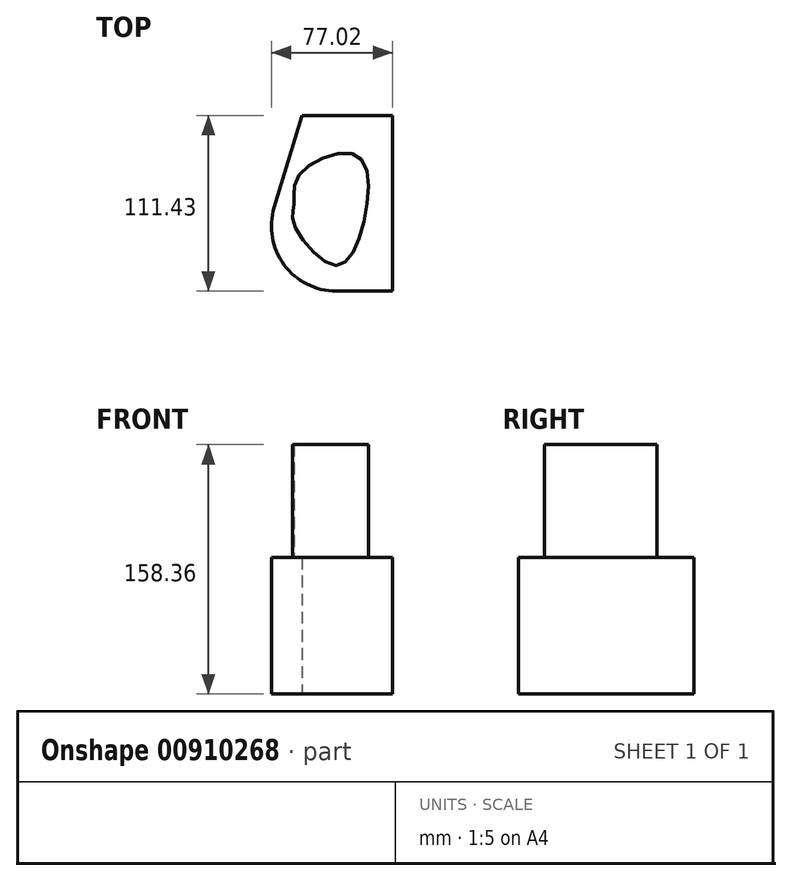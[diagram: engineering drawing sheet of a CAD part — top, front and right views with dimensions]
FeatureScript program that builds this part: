
annotation { "Feature Type Name" : "Feature", "Feature Type Description" : "" }
export const myFeature = defineFeature(function(context is Context, id is Id, definition is map)
    precondition{}
    {
        {
            var Q0;
            Q0=qCreatedBy(makeId("Top.planeOp"),FACE);
            var sketch = newSketch(context, id + "F0", { "sketchPlane" : qUnion([Q0])});
            skLineSegment(sketch, "E0", {"start": v(-54.44, -43.5) * mm, "end": v(36.9, -43.5) * mm});
            skLineSegment(sketch, "E1", {"start": v(36.9, -43.5) * mm, "end": v(36.9, 67.94) * mm});
            skLineSegment(sketch, "E2", {"start": v(36.9, 67.94) * mm, "end": v(-20.7, 67.94) * mm});
            skLineSegment(sketch, "E3", {"start": v(-20.7, 67.94) * mm, "end": v(-54.44, -43.5) * mm});
            skSolve(sketch);
        }
        {
            var Q0;
            Q0 = qSketchRegion(id + "F0", true);
            extrude(context, id + "F1", {"entities" : qUnion([Q0]), "depth" : 86.6 * mm, "offsetDistance" : 25.4 * mm});
        }
        {
            var Q0;
            Q0=makeQuery(id+"F1.opExtrude","SWEPT_EDGE",EDGE,{"disambiguationData":[OSD([sQuery(id+"F0.wireOp",EDGE,"E0"),sQuery(id+"F0.wireOp",EDGE,"E3")])]});
            fillet(context, id + "F2", {"entities" : qUnion([Q0]), "radius" : 41.2 * mm, "tangentPropagation" : true, "allowEdgeOverflow" : false});
        }
        {
            var Q0;
            Q0=makeQuery(id+"F1.opExtrude","CAP_FACE",FACE,{"disambiguationData":[OSD([sQuery(id+"F0.wireOp",EDGE,"E0"),sQuery(id+"F0.wireOp",EDGE,"E1"),sQuery(id+"F0.wireOp",EDGE,"E2"),sQuery(id+"F0.wireOp",EDGE,"E3")])],"isStart":false});
            var sketch = newSketch(context, id + "F3", { "sketchPlane" : qUnion([Q0])});
            skFitSpline(sketch, "E4", {"points": [v(-25.74, 11.32) * mm, v(-26, 0) * mm, v(0, -27.14) * mm, v(18.43, 0) * mm, v(13.81, 42.79) * mm, v(-22.64, 29.97) * mm, v(-25.74, 11.32) * mm]});
            skFitSpline(sketch, "E5", {"points": [v(0, 0) * mm, v(17.07, 67.94) * mm], "startDerivative": vector(17.07, 67.94) * mm, "endDerivative": vector(17.07, 67.94) * mm});
            skSolve(sketch);
        }
        {
            var Q0;
            Q0=makeQuery(id+"F3.imprint","IMPRINT",FACE,{"disambiguationData":[TD([[makeQuery(id+"F3.imprint","IMPRINT",EDGE,{"derivedFrom":sQuery(id+"F3.wireOp",EDGE,"E4")}),1.0]])]});
            extrude(context, id + "F4", {"entities" : qUnion([Q0]), "operationType" : NewBodyOperationType.ADD, "depth" : 71.77 * mm, "offsetDistance" : 25.4 * mm});
        }
    });
